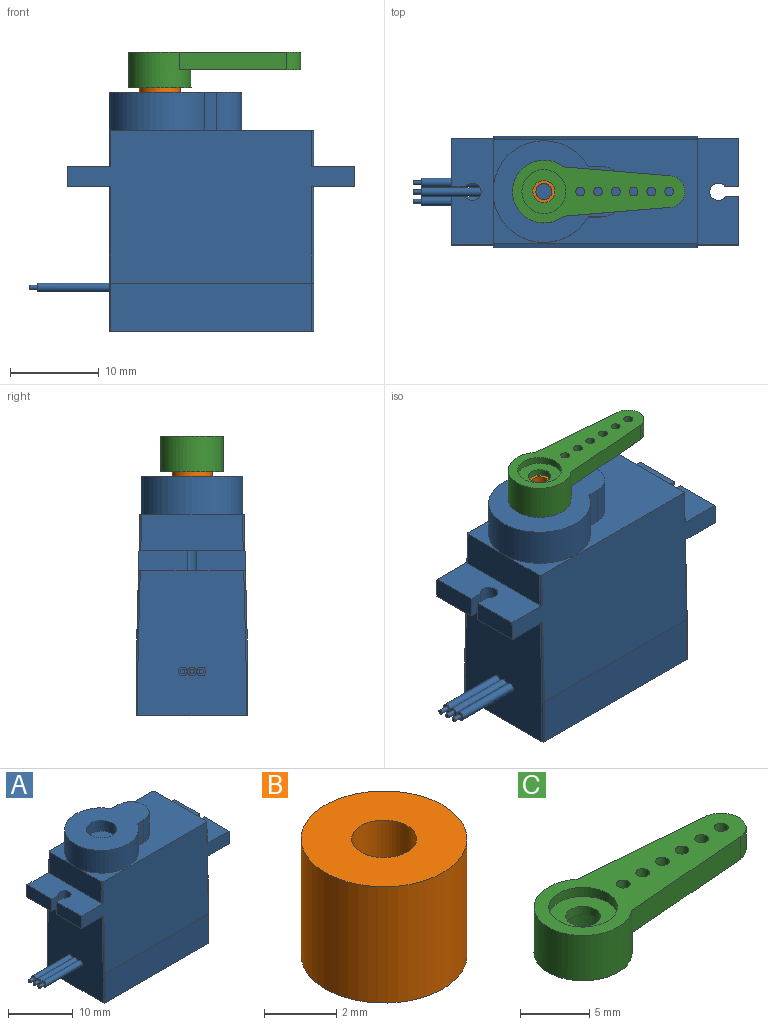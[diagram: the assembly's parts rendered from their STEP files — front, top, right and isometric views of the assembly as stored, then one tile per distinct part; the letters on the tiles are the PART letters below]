
ASSEMBLY  parts=3 mates=1
PART A: 75 faces, bbox 36.7x12.6x27 mm
  f0: plane 1x1mm, normal (-1,0,0), area 0.6mm2, adj f50,f55
  f1: plane 1x1mm, normal (-1,0,0), area 0.6mm2, adj f49,f53
  f2: plane 1x1mm, normal (-1,0,0), area 0.6mm2, adj f48,f51
  f3: plane 16.34x12.19mm, normal (-1,0,0), area 193.9mm2, adj f9,f17,f48,f49,f50,f61,f62,f63
  f4: plane 12.04x4.84mm, normal (0,0,-1), area 51.4mm2, adj f5,f13,f14,f24,f25,f29,f30,f31
  f5: plane 5.48x2.32mm, normal (1,0,0), area 12.6mm2, adj f4,f6,f25,f30
  f6: plane 11.93x4.84mm, normal (0,0,1), area 50.8mm2, adj f5,f14,f15,f24,f25,f29,f30,f31
  f7: plane 11.93x4.84mm, normal (0,0,1), area 50.8mm2, adj f8,f11,f12,f24,f25,f26,f27,f28
  f8: plane 5.48x2.32mm, normal (-1,0,0), area 12.6mm2, adj f7,f9,f24,f27
  f9: plane 12.04x4.84mm, normal (0,0,-1), area 51.4mm2, adj f3,f8,f12,f24,f25,f26,f27,f28
  f10: plane 23.03x11.72mm, normal (0,0,1), area 149mm2, adj f11,f15,f19,f20,f21,f22,f24,f25
  f11: plane 11.53x4.06mm, normal (-1,0,0), area 46.4mm2, adj f7,f10,f71,f72
  f12: plane 5.48x2.32mm, normal (-1,0,0), area 12.6mm2, adj f7,f9,f25,f28
  f13: plane 16.34x12.19mm, normal (1,0,0), area 196.2mm2, adj f4,f17,f65,f66,f67,f68
  f14: plane 5.48x2.32mm, normal (1,0,0), area 12.6mm2, adj f4,f6,f24,f31
  f15: plane 11.53x4.06mm, normal (1,0,0), area 46.4mm2, adj f6,f10,f69,f70
  f16: plane 22.63x5.5mm, normal (0,-1,0), area 124.5mm2, adj f17,f25,f61,f65
  f17: plane 23.03x12.59mm, normal (0,0,-1), area 277.3mm2, adj f3,f13,f16,f18,f32,f36,f40,f44
  f18: plane 22.63x5.5mm, normal (0,1,0), area 124.5mm2, adj f17,f24,f63,f67
  f19: cylinder r=5.72mm len=11.45mm, axis (0,0,-1), area 128.4mm2, adj f10,f20,f22,f23
  f20: plane 4.28x1.41mm, normal (0,-1,0), area 6mm2, adj f10,f19,f21,f23
  f21: cylinder r=2.85mm len=5.7mm, axis (0,0,-1), area 38.3mm2, adj f10,f20,f22,f23
  f22: plane 4.28x1.41mm, normal (0,1,0), area 6mm2, adj f10,f19,f21,f23
  f23: plane 14.95x11.45mm, normal (0,0,1), area 103.5mm2, adj f19,f20,f21,f22,f73
  f24: plane 32.31x17.22mm, normal (0,1,0.03), area 412.3mm2, adj f4,f6,f7,f8,f9,f10,f14,f18
  f25: plane 32.31x17.22mm, normal (0,-1,0.03), area 412.3mm2, adj f4,f5,f6,f7,f9,f10,f12,f16
  f26: cylinder r=0.97mm len=2.32mm, axis (0,0,-1), area 11.5mm2, adj f7,f9,f27,f28
  f27: plane 2.32x1.51mm, normal (0,-1,0), area 3.5mm2, adj f7,f8,f9,f26
  f28: plane 2.32x1.51mm, normal (0,1,0), area 3.5mm2, adj f7,f9,f12,f26
  f29: cylinder r=0.97mm len=2.32mm, axis (0,0,-1), area 11.5mm2, adj f4,f6,f30,f31
  f30: plane 2.32x1.51mm, normal (0,1,0), area 3.5mm2, adj f4,f5,f6,f29
  f31: plane 2.32x1.51mm, normal (0,-1,0), area 3.5mm2, adj f4,f6,f14,f29
  f32: cylinder r=1mm len=2mm, axis (0,0,-1), area 6.3mm2, adj f17,f33
  f33: plane 2x2mm, normal (0,0,-1), area 0.2mm2, adj f32,f34
  f34: cylinder r=0.97mm len=1.95mm, axis (0,0,-1), area 4.3mm2, adj f33,f60
  f35: plane 1.35x1.35mm, normal (0,0,-1), area 1.4mm2, adj f60
  f36: cylinder r=1mm len=2mm, axis (0,0,-1), area 6.3mm2, adj f17,f37
  f37: plane 2x2mm, normal (0,0,-1), area 0.2mm2, adj f36,f38
  f38: cylinder r=0.97mm len=1.95mm, axis (0,0,-1), area 4.3mm2, adj f37,f59
  f39: plane 1.35x1.35mm, normal (0,0,-1), area 1.4mm2, adj f59
  f40: cylinder r=1mm len=2mm, axis (0,0,-1), area 6.3mm2, adj f17,f41
  f41: plane 2x2mm, normal (0,0,-1), area 0.2mm2, adj f40,f42
  f42: cylinder r=0.97mm len=1.95mm, axis (0,0,-1), area 4.3mm2, adj f41,f57
  f43: plane 1.35x1.35mm, normal (0,0,-1), area 1.4mm2, adj f57
  f44: cylinder r=1mm len=2mm, axis (0,0,-1), area 6.3mm2, adj f17,f45
  f45: plane 2x2mm, normal (0,0,-1), area 0.2mm2, adj f44,f46
  f46: cylinder r=0.97mm len=1.95mm, axis (0,0,-1), area 4.3mm2, adj f45,f58
  f47: plane 1.35x1.35mm, normal (0,0,-1), area 1.4mm2, adj f58
  f48: cylinder r=0.5mm len=8mm, axis (1,0,0), area 25.1mm2, adj f2,f3
  f49: cylinder r=0.5mm len=8mm, axis (1,0,0), area 25.1mm2, adj f1,f3
  f50: cylinder r=0.5mm len=8mm, axis (1,0,0), area 25.1mm2, adj f0,f3
  f51: cylinder r=0.25mm len=1mm, axis (1,0,0), area 1.6mm2, adj f2,f52
  f52: plane 0.5x0.5mm, normal (-1,0,0), area 0.2mm2, adj f51
  f53: cylinder r=0.25mm len=1mm, axis (1,0,0), area 1.6mm2, adj f1,f54
  f54: plane 0.5x0.5mm, normal (-1,0,0), area 0.2mm2, adj f53
  f55: cylinder r=0.25mm len=1mm, axis (1,0,0), area 1.6mm2, adj f0,f56
  f56: plane 0.5x0.5mm, normal (-1,0,0), area 0.2mm2, adj f55
  f57: torus R=0.68mm, axis (0,0,1), area 2.6mm2, adj f42,f43
  f58: torus R=0.68mm, axis (0,0,1), area 2.6mm2, adj f46,f47
  f59: torus R=0.68mm, axis (0,0,1), area 2.6mm2, adj f38,f39
  f60: torus R=0.68mm, axis (0,0,1), area 2.6mm2, adj f34,f35
  f61: cylinder r=0.2mm len=5.5mm, axis (0,0,1), area 1.7mm2, adj f3,f16,f17,f62
  f62: cylinder r=0.2mm len=10.85mm, axis (0,0.03,1), area 3.4mm2, adj f3,f9,f25,f61
  f63: cylinder r=0.2mm len=5.5mm, axis (0,0,-1), area 1.7mm2, adj f3,f17,f18,f64
  f64: cylinder r=0.2mm len=10.85mm, axis (0,0.03,-1), area 3.4mm2, adj f3,f9,f24,f63
  f65: cylinder r=0.2mm len=5.5mm, axis (0,0,-1), area 1.7mm2, adj f13,f16,f17,f66
  f66: cylinder r=0.2mm len=10.85mm, axis (0,-0.03,-1), area 3.4mm2, adj f4,f13,f25,f65
  f67: cylinder r=0.2mm len=5.5mm, axis (0,0,1), area 1.7mm2, adj f13,f17,f18,f68
  f68: cylinder r=0.2mm len=10.85mm, axis (0,-0.03,1), area 3.4mm2, adj f4,f13,f24,f67
  f69: cylinder r=0.2mm len=4.07mm, axis (0,-0.03,1), area 1.3mm2, adj f6,f10,f15,f24
  f70: cylinder r=0.2mm len=4.07mm, axis (0,-0.03,-1), area 1.3mm2, adj f6,f10,f15,f25
  f71: cylinder r=0.2mm len=4.07mm, axis (0,0.03,-1), area 1.3mm2, adj f7,f10,f11,f24
  f72: cylinder r=0.2mm len=4.07mm, axis (0,0.03,1), area 1.3mm2, adj f7,f10,f11,f25
  f73: cylinder r=2.35mm len=4.7mm, axis (0,0,1), area 30.3mm2, adj f23,f74
  f74: plane 4.7x4.7mm, normal (0,0,1), area 17.3mm2, adj f73
PART B: 4 faces, bbox 4.6x4.6x4 mm
  f0: cylinder r=2.3mm len=4.6mm, axis (0,0,1), area 57.1mm2, adj f1,f3
  f1: plane 4.6x4.6mm, normal (0,0,-1), area 14.1mm2, adj f0,f2
  f2: cylinder r=0.9mm len=3.95mm, axis (0,0,1), area 22.3mm2, adj f1,f3
  f3: plane 4.6x4.6mm, normal (0,0,1), area 14.1mm2, adj f0,f2
PART C: 18 faces, bbox 19.4x7.1x4 mm
  f0: cylinder r=3.54mm len=7.07mm, axis (0,0,1), area 76.1mm2, adj f1,f7,f9,f16,f17
  f1: plane 19.4x7.07mm, normal (0,0,1), area 69.3mm2, adj f0,f2,f8,f9,f10,f11,f12,f13
  f2: cylinder r=2.48mm len=4.95mm, axis (0,0,1), area 12.4mm2, adj f1,f3
  f3: plane 4.95x4.95mm, normal (0,0,1), area 14.4mm2, adj f2,f4
  f4: cylinder r=1.25mm len=2.49mm, axis (0,0,1), area 5.9mm2, adj f3,f5
  f5: plane 4.75x4.75mm, normal (0,0,-1), area 12.9mm2, adj f4,f6
  f6: cylinder r=2.38mm len=4.75mm, axis (0,0,1), area 36.6mm2, adj f5,f7
  f7: plane 7.07x7.07mm, normal (0,0,-1), area 21.5mm2, adj f0,f6
  f8: cylinder r=0.5mm len=2mm, axis (0,0,-1), area 6.3mm2, adj f1,f16
  f9: plane 12.04x2mm, normal (0.08,-1,0), area 24.2mm2, adj f0,f1,f10,f16
  f10: cylinder r=1.78mm len=3.55mm, axis (0,0,-1), area 10.6mm2, adj f1,f9,f16,f17
  f11: cylinder r=0.5mm len=2mm, axis (0,0,-1), area 6.3mm2, adj f1,f16
  f12: cylinder r=0.5mm len=2mm, axis (0,0,-1), area 6.3mm2, adj f1,f16
  f13: cylinder r=0.5mm len=2mm, axis (0,0,-1), area 6.3mm2, adj f1,f16
  f14: cylinder r=0.5mm len=2mm, axis (0,0,-1), area 6.3mm2, adj f1,f16
  f15: cylinder r=0.5mm len=2mm, axis (0,0,-1), area 6.3mm2, adj f1,f16
  f16: plane 13.68x5.55mm, normal (0,0,-1), area 49.3mm2, adj f0,f8,f9,f10,f11,f12,f13,f14
  f17: plane 12.04x2mm, normal (0.08,1,0), area 24.2mm2, adj f0,f1,f10,f16
PLACE A t=(-7.91,8.8,3.3)mm
PLACE B t=(-7.91,8.8,3.3)mm
PLACE C t=(-9.32,8.8,16.46)mm
MATE revolute C.f0 <-> B.f0  axis (0,0,-1) through (-9.32,8.8,16.91)mm
